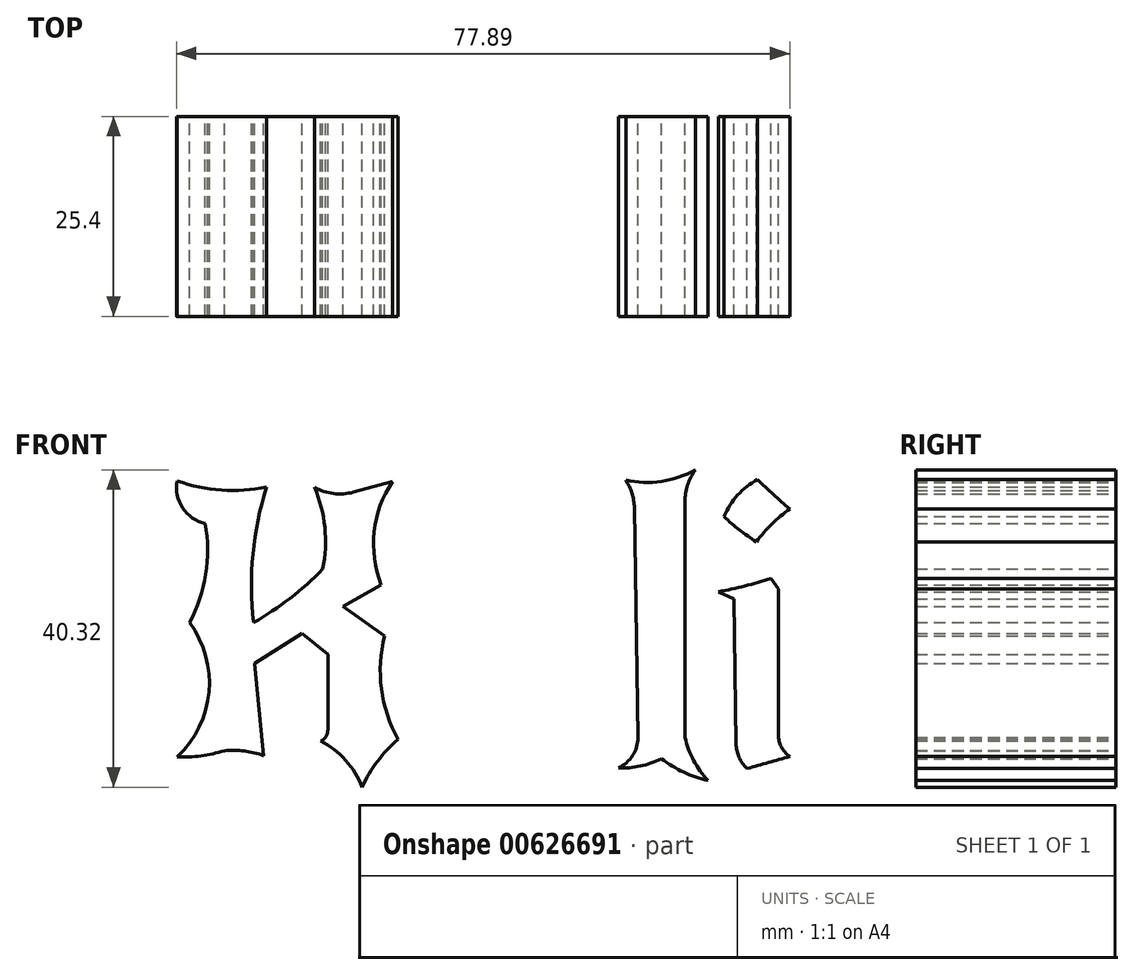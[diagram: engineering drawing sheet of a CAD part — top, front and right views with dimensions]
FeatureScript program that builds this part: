
annotation { "Feature Type Name" : "Feature", "Feature Type Description" : "" }
export const myFeature = defineFeature(function(context is Context, id is Id, definition is map)
    precondition{}
    {
        {
            var Q0;
            Q0=qCreatedBy(makeId("Front.planeOp"),FACE);
            var sketch = newSketch(context, id + "F0", { "sketchPlane" : qUnion([Q0])});
            skLineSegment(sketch, "E0", {"start": v(-34.42, 33.26) * mm, "end": v(-28.42, 37.12) * mm});
            skLineSegment(sketch, "E1", {"start": v(-28.42, 37.12) * mm, "end": v(-25.14, 34.4) * mm});
            skLineSegment(sketch, "E2", {"start": v(-25.14, 34.4) * mm, "end": v(-25.14, 24.77) * mm});
            skLineSegment(sketch, "E3", {"start": v(-34.42, 33.26) * mm, "end": v(-33.28, 21.55) * mm});
            skLineSegment(sketch, "E4", {"start": v(-18.35, 43.26) * mm, "end": v(-23.2, 40.55) * mm});
            skLineSegment(sketch, "E5", {"start": v(-23.2, 40.55) * mm, "end": v(-17.92, 36.76) * mm});
            skArc(sketch, "E6", {"start": v(-17.92, 36.76) * mm, "mid": v(-18.33, 30.03) * mm, "end": v(-16.2, 23.62) * mm});
            skArc(sketch, "E7", {"start": v(-16.92, 56.4) * mm, "mid": v(-19.24, 50) * mm, "end": v(-18.35, 43.26) * mm});
            skLineSegment(sketch, "E8", {"start": v(-16.92, 56.4) * mm, "end": v(-21.85, 55.04) * mm});
            skArc(sketch, "E9", {"start": v(-26.85, 55.68) * mm, "mid": v(-24.41, 54.86) * mm, "end": v(-21.85, 55.04) * mm});
            skArc(sketch, "E10", {"start": v(-25.78, 45.26) * mm, "mid": v(-25.51, 50.55) * mm, "end": v(-26.85, 55.68) * mm});
            skArc(sketch, "E11", {"start": v(-34.56, 38.48) * mm, "mid": v(-29.93, 41.56) * mm, "end": v(-25.78, 45.26) * mm});
            skArc(sketch, "E12", {"start": v(-32.92, 55.68) * mm, "mid": v(-34.64, 47.17) * mm, "end": v(-34.56, 38.48) * mm});
            skArc(sketch, "E13", {"start": v(-44.27, 56.47) * mm, "mid": v(-38.65, 55.3) * mm, "end": v(-32.92, 55.68) * mm});
            skArc(sketch, "E14", {"start": v(-44.27, 56.47) * mm, "mid": v(-43.58, 53.04) * mm, "end": v(-40.7, 51.04) * mm});
            skArc(sketch, "E15", {"start": v(-42.7, 38.48) * mm, "mid": v(-40.66, 44.6) * mm, "end": v(-40.7, 51.04) * mm});
            skArc(sketch, "E16", {"start": v(-44.27, 21.41) * mm, "mid": v(-40.24, 29.64) * mm, "end": v(-42.7, 38.48) * mm});
            skArc(sketch, "E17", {"start": v(-44.27, 21.41) * mm, "mid": v(-41.24, 21.53) * mm, "end": v(-38.27, 22.2) * mm});
            skArc(sketch, "E18", {"start": v(-33.28, 21.55) * mm, "mid": v(-35.74, 22.15) * mm, "end": v(-38.27, 22.2) * mm});
            skArc(sketch, "E19", {"start": v(-26.06, 23.41) * mm, "mid": v(-25.39, 23.95) * mm, "end": v(-25.14, 24.77) * mm});
            skArc(sketch, "E20", {"start": v(-20.78, 17.56) * mm, "mid": v(-22.87, 20.98) * mm, "end": v(-26.06, 23.41) * mm});
            skArc(sketch, "E21", {"start": v(-16.2, 23.62) * mm, "mid": v(-18.82, 20.84) * mm, "end": v(-20.78, 17.56) * mm});
            skLineSegment(sketch, "E22", {"start": v(-3.15, 27.16) * mm, "end": v(1.38, 29.24) * mm});
            skLineSegment(sketch, "E23", {"start": v(1.38, 29.24) * mm, "end": v(1.38, 39.5) * mm});
            skArc(sketch, "E24", {"start": v(1.38, 39.5) * mm, "mid": v(0.75, 40.87) * mm, "end": v(-0.7, 41.3) * mm});
            skLineSegment(sketch, "E25", {"start": v(-0.7, 41.3) * mm, "end": v(-0.7, 42.22) * mm});
            skArc(sketch, "E26", {"start": v(-0.7, 42.22) * mm, "mid": v(3.36, 42.62) * mm, "end": v(7.1, 44.19) * mm});
            skLineSegment(sketch, "E27", {"start": v(7.1, 44.19) * mm, "end": v(7.55, 14.64) * mm});
            skArc(sketch, "E28", {"start": v(7.55, 14.64) * mm, "mid": v(1.41, 12.7) * mm, "end": v(-3.99, 9.2) * mm});
            skArc(sketch, "E29", {"start": v(-3.99, 9.2) * mm, "mid": v(-8.44, 11.89) * mm, "end": v(-13.53, 12.99) * mm});
            skArc(sketch, "E30", {"start": v(-10.72, 19.08) * mm, "mid": v(-12.68, 16.25) * mm, "end": v(-13.6, 12.93) * mm});
            skArc(sketch, "E31", {"start": v(-1.92, 14.64) * mm, "mid": v(-6.12, 17.26) * mm, "end": v(-10.72, 19.08) * mm});
            skLineSegment(sketch, "E32", {"start": v(-1.92, 14.64) * mm, "end": v(1.65, 15.69) * mm});
            skLineSegment(sketch, "E33", {"start": v(1.65, 15.69) * mm, "end": v(1.65, 25.92) * mm});
            skArc(sketch, "E34", {"start": v(1.65, 25.92) * mm, "mid": v(-2.43, 23.9) * mm, "end": v(-5.83, 20.86) * mm});
            skArc(sketch, "E35", {"start": v(-5.83, 20.86) * mm, "mid": v(-8.6, 23.1) * mm, "end": v(-11.7, 24.83) * mm});
            skArc(sketch, "E36", {"start": v(-11.7, 24.83) * mm, "mid": v(-10.95, 31.48) * mm, "end": v(-11.12, 38.17) * mm});
            skArc(sketch, "E37", {"start": v(-11.12, 38.17) * mm, "mid": v(-12, 40.14) * mm, "end": v(-13.36, 41.8) * mm});
            skArc(sketch, "E38", {"start": v(-13.36, 41.8) * mm, "mid": v(-9.12, 42.8) * mm, "end": v(-4.9, 43.98) * mm});
            skLineSegment(sketch, "E39", {"start": v(-4.9, 43.98) * mm, "end": v(-5.43, 28.57) * mm});
            skLineSegment(sketch, "E40", {"start": v(-5.43, 28.57) * mm, "end": v(-3.15, 27.16) * mm});
            skLineSegment(sketch, "E41", {"start": v(13.8, 53.05) * mm, "end": v(14.24, 23.9) * mm});
            skArc(sketch, "E42", {"start": v(11.76, 20) * mm, "mid": v(13.58, 21.58) * mm, "end": v(14.24, 23.9) * mm});
            skArc(sketch, "E43", {"start": v(11.76, 20) * mm, "mid": v(14.58, 20.24) * mm, "end": v(17.24, 21.18) * mm});
            skArc(sketch, "E44", {"start": v(17.24, 21.18) * mm, "mid": v(20.05, 19.47) * mm, "end": v(23.16, 18.4) * mm});
            skArc(sketch, "E45", {"start": v(20.24, 23.9) * mm, "mid": v(21.34, 20.95) * mm, "end": v(23.16, 18.4) * mm});
            skLineSegment(sketch, "E46", {"start": v(20.24, 23.9) * mm, "end": v(20.24, 53.78) * mm});
            skArc(sketch, "E47", {"start": v(21.55, 57.88) * mm, "mid": v(20.58, 55.93) * mm, "end": v(20.24, 53.78) * mm});
            skArc(sketch, "E48", {"start": v(12.7, 56.56) * mm, "mid": v(17.25, 56.4) * mm, "end": v(21.55, 57.88) * mm});
            skArc(sketch, "E49", {"start": v(13.8, 53.05) * mm, "mid": v(13.51, 54.89) * mm, "end": v(12.7, 56.56) * mm});
            skArc(sketch, "E50", {"start": v(33.54, 52.9) * mm, "mid": v(31.26, 50.99) * mm, "end": v(29.3, 48.74) * mm});
            skArc(sketch, "E51", {"start": v(29.45, 56.63) * mm, "mid": v(31.46, 54.73) * mm, "end": v(33.54, 52.9) * mm});
            skArc(sketch, "E52", {"start": v(29.45, 56.63) * mm, "mid": v(26.93, 54.66) * mm, "end": v(25.2, 51.95) * mm});
            skArc(sketch, "E53", {"start": v(25.2, 51.95) * mm, "mid": v(27.16, 50.22) * mm, "end": v(29.3, 48.74) * mm});
            skArc(sketch, "E54", {"start": v(24.48, 42.38) * mm, "mid": v(27.83, 43.12) * mm, "end": v(31.13, 44.06) * mm});
            skLineSegment(sketch, "E55", {"start": v(24.48, 42.38) * mm, "end": v(26.45, 41.5) * mm});
            skLineSegment(sketch, "E56", {"start": v(26.45, 41.5) * mm, "end": v(26.73, 23.08) * mm});
            skLineSegment(sketch, "E57", {"start": v(31.13, 44.06) * mm, "end": v(32.08, 42.74) * mm});
            skLineSegment(sketch, "E58", {"start": v(32.08, 42.74) * mm, "end": v(32.08, 24.25) * mm});
            skArc(sketch, "E59", {"start": v(32.08, 24.25) * mm, "mid": v(32.47, 22.68) * mm, "end": v(33.54, 21.47) * mm});
            skArc(sketch, "E60", {"start": v(28.13, 19.93) * mm, "mid": v(30.85, 20.67) * mm, "end": v(33.54, 21.47) * mm});
            skArc(sketch, "E61", {"start": v(26.73, 23.08) * mm, "mid": v(27.1, 21.36) * mm, "end": v(28.13, 19.93) * mm});
            skArc(sketch, "E62", {"start": v(37.71, 39.82) * mm, "mid": v(41.24, 41.52) * mm, "end": v(44.22, 44.06) * mm});
            skArc(sketch, "E63", {"start": v(44.22, 44.2) * mm, "mid": v(49.27, 43.39) * mm, "end": v(54.38, 43.18) * mm});
            skArc(sketch, "E64", {"start": v(54.38, 43.18) * mm, "mid": v(54.69, 37.95) * mm, "end": v(55.62, 32.8) * mm});
            skArc(sketch, "E65", {"start": v(55.62, 32.8) * mm, "mid": v(49.96, 31.82) * mm, "end": v(44.3, 30.83) * mm});
            skLineSegment(sketch, "E66", {"start": v(44.3, 30.83) * mm, "end": v(43.56, 26.15) * mm});
            skLineSegment(sketch, "E67", {"start": v(43.56, 26.15) * mm, "end": v(50.54, 25.06) * mm});
            skArc(sketch, "E68", {"start": v(54.67, 28.85) * mm, "mid": v(52.01, 27.6) * mm, "end": v(50.54, 25.06) * mm});
            skArc(sketch, "E69", {"start": v(55.34, 22.86) * mm, "mid": v(50.9, 21.73) * mm, "end": v(46.78, 19.71) * mm});
            skArc(sketch, "E70", {"start": v(46.78, 19.71) * mm, "mid": v(42.23, 21.8) * mm, "end": v(37.35, 22.86) * mm});
            skArc(sketch, "E71", {"start": v(37.2, 22.86) * mm, "mid": v(38.43, 31.3) * mm, "end": v(37.71, 39.82) * mm});
            skLineSegment(sketch, "E72", {"start": v(48.9, 38.94) * mm, "end": v(49.48, 34.85) * mm});
            skLineSegment(sketch, "E73", {"start": v(49.48, 34.85) * mm, "end": v(44.3, 33.77) * mm});
            skLineSegment(sketch, "E74", {"start": v(44.3, 33.77) * mm, "end": v(43.85, 39.82) * mm});
            skLineSegment(sketch, "E75", {"start": v(54.67, 28.85) * mm, "end": v(55.34, 22.86) * mm});
            skLineSegment(sketch, "E76", {"start": v(43.85, 39.82) * mm, "end": v(48.9, 38.94) * mm});
            skSolve(sketch);
        }
        {
            var Q0;
            Q0=makeQuery(id+"F0.imprint","IMPRINT",FACE,{"disambiguationData":[TD([[makeQuery(id+"F0.imprint","IMPRINT",EDGE,{"derivedFrom":sQuery(id+"F0.wireOp",EDGE,"E0")}),1.0]])]});
            var Q1;
            Q1=makeQuery(id+"F0.imprint","IMPRINT",FACE,{"disambiguationData":[TD([[makeQuery(id+"F0.imprint","IMPRINT",EDGE,{"derivedFrom":sQuery(id+"F0.wireOp",EDGE,"E41")}),1.0]])]});
            var Q2;
            Q2=makeQuery(id+"F0.imprint","IMPRINT",FACE,{"disambiguationData":[TD([[makeQuery(id+"F0.imprint","IMPRINT",EDGE,{"derivedFrom":sQuery(id+"F0.wireOp",EDGE,"E54")}),-1.0]])]});
            var Q3;
            Q3=makeQuery(id+"F0.imprint","IMPRINT",FACE,{"disambiguationData":[TD([[makeQuery(id+"F0.imprint","IMPRINT",EDGE,{"derivedFrom":sQuery(id+"F0.wireOp",EDGE,"E50")}),-1.0]])]});
            extrude(context, id + "F1", {"entities" : qUnion([Q0, Q1, Q2, Q3]), "depth" : 25.4 * mm, "offsetDistance" : 25.4 * mm});
        }
    });
